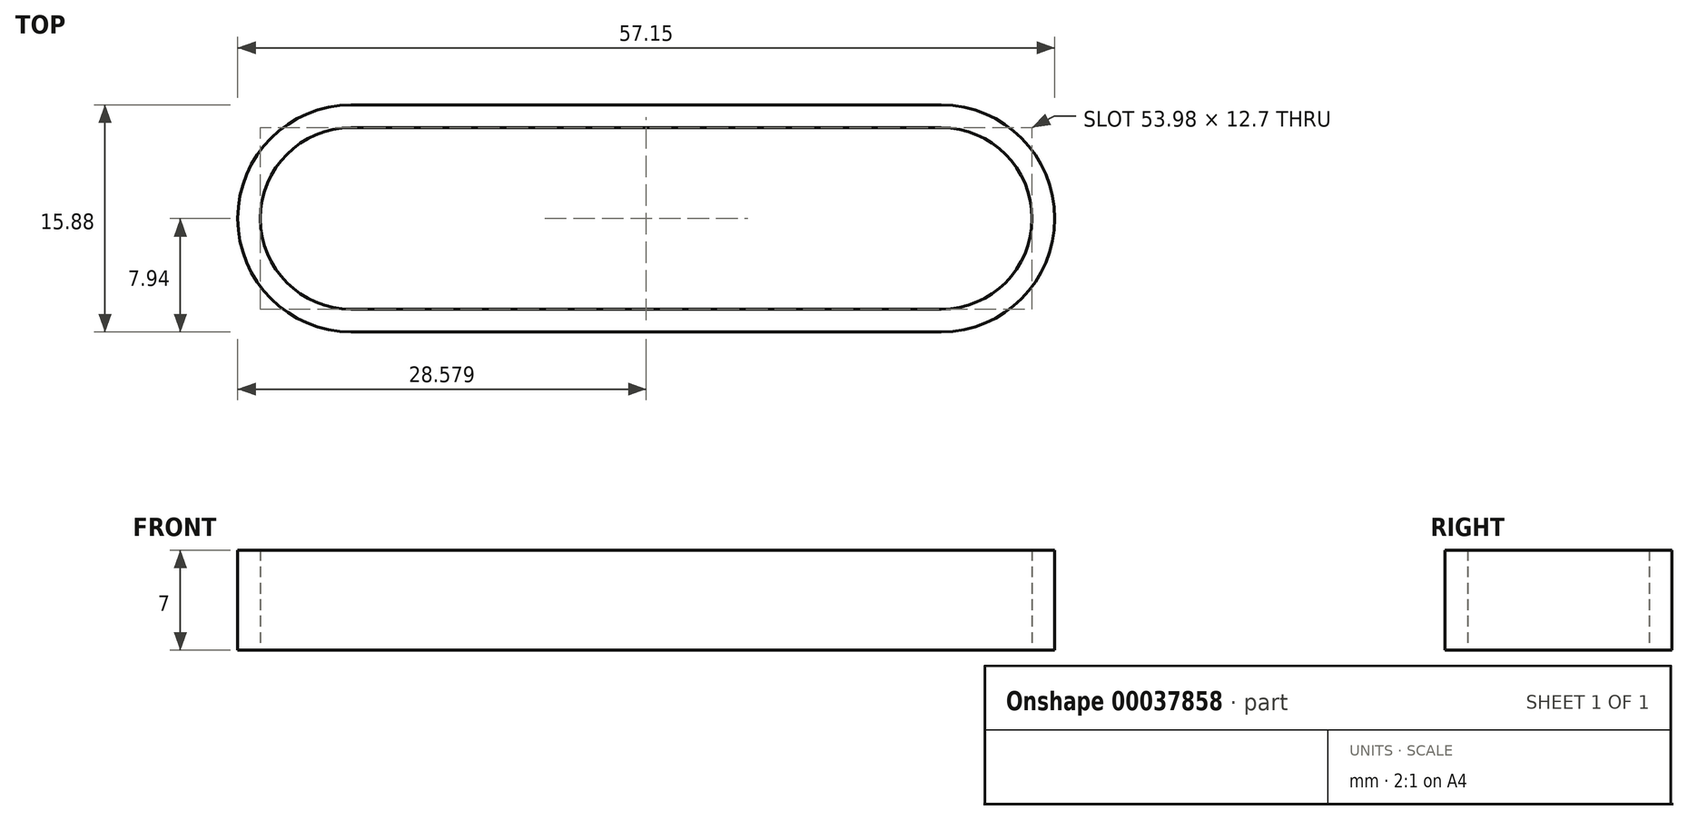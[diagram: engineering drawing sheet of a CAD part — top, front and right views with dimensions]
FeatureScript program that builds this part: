
annotation { "Feature Type Name" : "Feature", "Feature Type Description" : "" }
export const myFeature = defineFeature(function(context is Context, id is Id, definition is map)
    precondition{}
    {
        {
            var Q0;
            Q0=qCreatedBy(makeId("Top.planeOp"),FACE);
            var sketch = newSketch(context, id + "F0", { "sketchPlane" : qUnion([Q0])});
            skLineSegment(sketch, "E0.bottom", {"start": v(0, 0) * mm, "end": v(41.28, 0) * mm});
            skLineSegment(sketch, "E0.top", {"start": v(0, 12.7) * mm, "end": v(41.28, 12.7) * mm});
            skLineSegment(sketch, "E0.left", {"start": v(0, 0) * mm, "end": v(0, 12.7) * mm, "construction": true});
            skLineSegment(sketch, "E0.right", {"start": v(41.28, 0) * mm, "end": v(41.28, 12.7) * mm, "construction": true});
            skArc(sketch, "E1", {"start": v(0, 12.7) * mm, "mid": v(-6.35, 6.35) * mm, "end": v(0, 0) * mm});
            skArc(sketch, "E2", {"start": v(41.28, 0) * mm, "mid": v(47.63, 6.35) * mm, "end": v(41.28, 12.7) * mm});
            skLineSegment(sketch, "E3", {"start": v(20.64, 0) * mm, "end": v(20.64, -1.59) * mm, "construction": true});
            skLineSegment(sketch, "E4", {"start": v(20.64, 12.7) * mm, "end": v(20.64, 14.29) * mm, "construction": true});
            skLineSegment(sketch, "E5", {"start": v(0, 14.29) * mm, "end": v(41.28, 14.29) * mm});
            skLineSegment(sketch, "E6", {"start": v(0, -1.59) * mm, "end": v(41.28, -1.59) * mm});
            skArc(sketch, "E7", {"start": v(0, 14.29) * mm, "mid": v(-7.94, 6.35) * mm, "end": v(0, -1.59) * mm});
            skArc(sketch, "E8", {"start": v(41.28, -1.59) * mm, "mid": v(49.21, 6.35) * mm, "end": v(41.28, 14.29) * mm});
            skLineSegment(sketch, "E9", {"start": v(0, 6.35) * mm, "end": v(4.38, -6.36) * mm, "construction": true});
            skLineSegment(sketch, "E10", {"start": v(4.38, -6.36) * mm, "end": v(41.28, 6.35) * mm, "construction": true});
            skSolve(sketch);
        }
        {
            var Q0;
            Q0 = qSketchRegion(id + "F0", true);
            extrude(context, id + "F1", {"entities" : qUnion([Q0]), "depth" : 7 * mm});
        }
    });
